# Revit family: Access_Door-Heavy_Duty-Best Access Doors-Double_Leaf-(BA-LO2D)
name_source: partatom
category: Specialty Equipment
revit_build: Autodesk Revit 2017 (Build: 20160225_1515(x64)
units: mm (PartAtom-declared; Revit-internal decimal feet)

## family parameters
Cut with Voids When Loaded = No
Host = Face
OmniClass Number = 23.30.10.27.17
Part Type = Normal
Room Calculation Point = No
Round Connector Dimension = Use Diameter
Shared = No

## types (2) — shared parameters
Assembly Code = C1020700
Construction Material = Metal - Best Access Doors - Aluminum
Default Elevation = 0"
Description = Heavy duty access door with double leaf for large openings
Finish = Metal - Best Access Doors - Powder Coated White
Frame Depth = 2 1/2"
Manufacturer = Best Access Doors
Model = BA-LO2D
Product data url = https://bimobject.com

## per-type parameters (varying)
| type | Door Height | Door Height Calc | Door Width | Door Width Calc | Height Actual | Panel Height | Panel Width | URL | Width Actual |
| 48 x 48 | 24" | 24" | 24" | 24" | 26" | 12" | 12" | https://www.bestaccessdoors.com | 26" |
| Custom | 48" | 48" | 48" | 48" | 50" | 24" | 24" | http://www.bestaccessdoors.com | 50" |

## geometry (parser evidence)
native form markers: Blend x4, Sweep x9
no freeform markers — native parametric forms only
